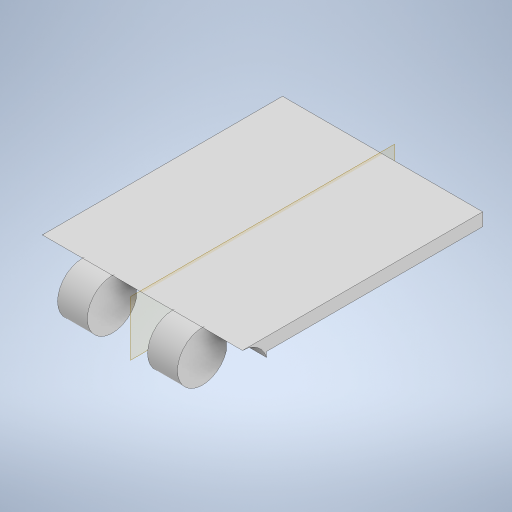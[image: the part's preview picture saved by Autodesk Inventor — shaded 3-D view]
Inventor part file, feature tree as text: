
AUTODESK INVENTOR PART (.ipt)
format: ipt  version: 2024.2 (Build 282272000, 272)  size: 289,280 bytes
history: native  units: in
note: dims shown in document units (in); Inventor stores cm internally (conversion verified against a paired STEP export)
features: sketch x7, extrude x5, revolve x2, plane x1, mirror x1
ambient origin geometry x8: Origin, YZ Plane, XZ Plane, XY Plane, X Axis, Y Axis, Z Axis, Center Point
bodies: Solid1 (feature_tree)
feature tree (16):
  extrude  "Extrusion1"  Depth=3.0in
  extrude  "Extrusion2"  Depth=0.5in TaperAngle=0.0deg
  plane  "Work Plane1"
  mirror  "Mirror1"
  revolve  "Revolution1"  [1 undecoded]
  revolve  "Revolution2"  Angle=90.0deg
  extrude  "Extrusion3"  Depth=0.65in
  extrude  "Extrusion4"  Depth=0.161in
  extrude  "Extrusion5"  Depth=2.7in TaperAngle=0.0deg
  sketch  "Sketch1"  dims[d0=2.5in d1=3.0in]
  sketch  "Sketch2"  dims[d2=0.625in d3=0.0in d5=0.5in d6=0.0in]
  sketch  "Sketch3"  dims[d7=-1.25in d8=0.75in]
  sketch  "Sketch4"  dims[d9=0.375in d10=90.0deg]
  sketch  "Sketch5"  dims[d11=90.0deg d12=0.65in]
  sketch  "Sketch6"  dims[d13=0.0in d14=0.0in d15=0.161in]
  sketch  "Sketch7"  dims[d16=2.7in d17=1.0in d18=0.0in d19=0.0in d20=0.0in]
note: 1 required parameter value undecoded (feature->parameter linkage not recoverable at this tier; creation-order binding heuristic only, values carry confidence <= 0.55)
